# Revit family: Basin-Caroma Opal 510 Wall Vanity
name_source: partatom
category: Plumbing Fixtures
revit_build: Autodesk Revit Architecture 2012 (Build: 20110309_2315(x64)
units: mm (PartAtom-declared; Revit-internal decimal feet)

## types (6) — shared parameters
CW Connection = No
Default Elevation = 786 mm  [stored 2.57874 ft]
Description = Opal 510 Wall Basin
HW Connection = No
Manufacturer = Caroma
PlumbingMaterial_ANZRS = Porcelain-White-Caroma
Type Comments = Ceramic Wall Basin
URL = www.caroma.com.au
Vent Connection = No
Waste = Metal-Chrome-Caroma
Waste Connection = Yes

## per-type parameters (varying)
| type | 1 Taphole | 3 Tapholes | Model | Shroud | Spout Penetration | Tap Penetrations |
| Opal 510 - 3 Tap Holes with Shroud | No | Yes | 632630 | Yes | 0 mm  [stored 0 ft] | 0 mm  [stored 0 ft] |
| Opal 510 - 1 Tap Hole with Shroud | Yes | No | 632610 | Yes | 0 mm  [stored 0 ft] | 100 mm  [stored 0.328084 ft] |
| Opal 510 - 0 Tap Holes with Shroud | No | No | 632600 | Yes | 100 mm  [stored 0.328084 ft] | 100 mm  [stored 0.328084 ft] |
| Opal 510 - 3 Tap Holes without Shroud | No | Yes | 632630 | No | 0 mm  [stored 0 ft] | 0 mm  [stored 0 ft] |
| Opal 510 - 1 Tap Hole without Shroud | Yes | No | 632610 | No | 0 mm  [stored 0 ft] | 100 mm  [stored 0.328084 ft] |
| Opal 510 - 0 Tap Holes without Shroud | No | No | 632600 | No | 100 mm  [stored 0.328084 ft] | 100 mm  [stored 0.328084 ft] |

note: [stored X ft] marks values corroborated as IEEE doubles in the binary element streams (Revit-internal decimal feet)

## geometry (parser evidence)
native form markers: Blend x8, Sweep x4
no freeform markers — native parametric forms only
